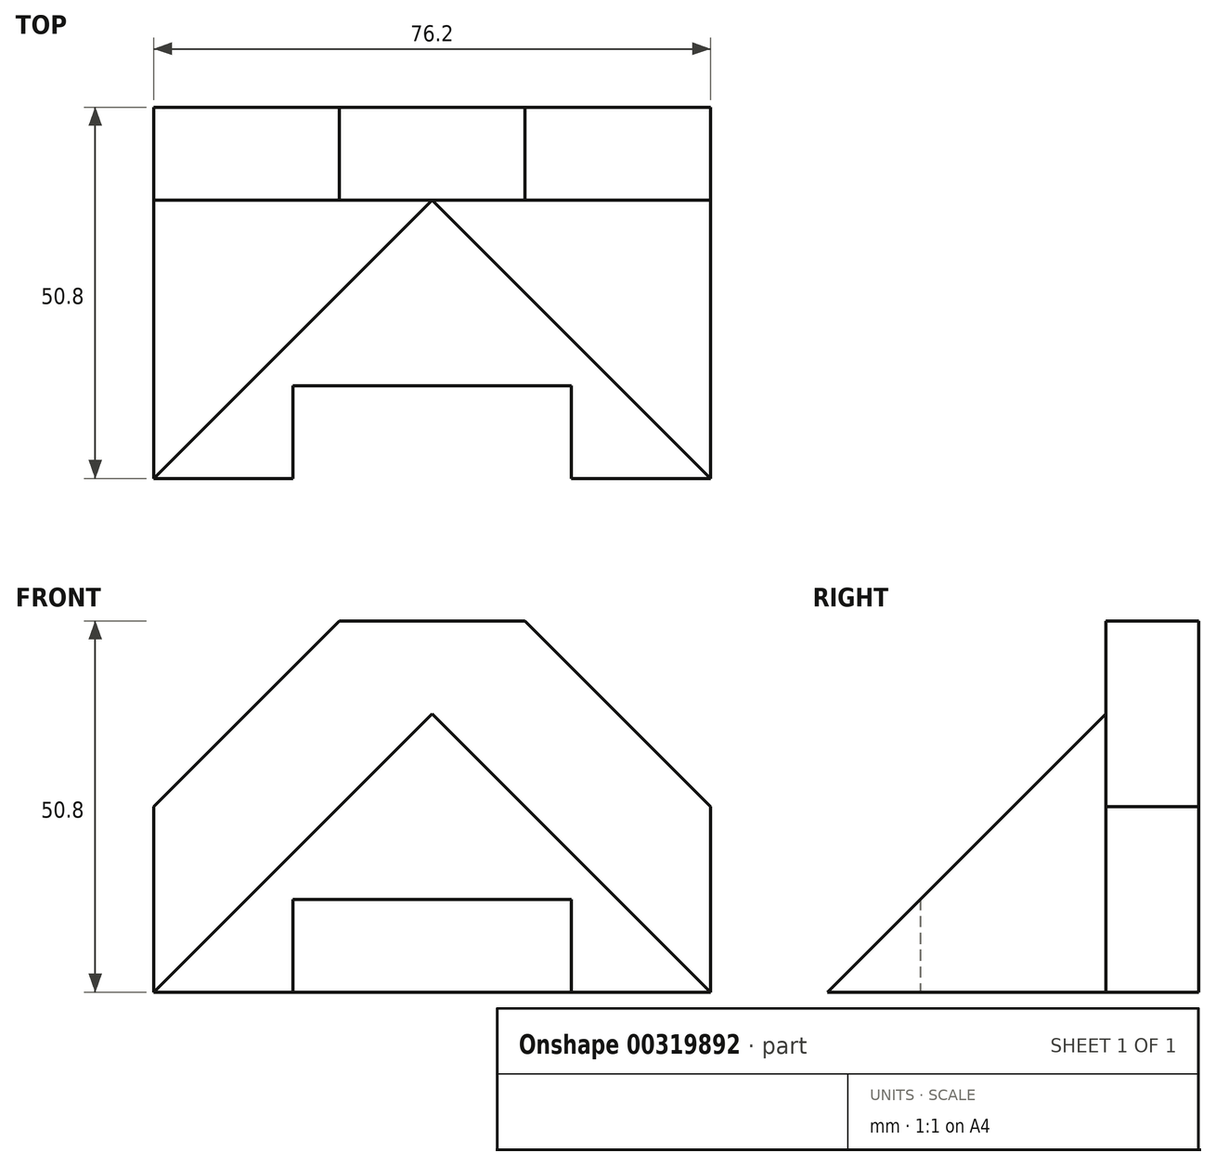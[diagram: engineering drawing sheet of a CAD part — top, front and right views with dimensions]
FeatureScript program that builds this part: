
annotation { "Feature Type Name" : "Feature", "Feature Type Description" : "" }
export const myFeature = defineFeature(function(context is Context, id is Id, definition is map)
    precondition{}
    {
        {
            var Q0;
            Q0=qCreatedBy(makeId("Front.planeOp"),FACE);
            var sketch = newSketch(context, id + "F0", { "sketchPlane" : qUnion([Q0])});
            skLineSegment(sketch, "E0", {"start": v(0, 0) * mm, "end": v(0, 50.8) * mm});
            skLineSegment(sketch, "E1", {"start": v(0, 50.8) * mm, "end": v(76.2, 50.8) * mm});
            skLineSegment(sketch, "E2", {"start": v(76.2, 50.8) * mm, "end": v(76.2, 0) * mm});
            skLineSegment(sketch, "E3", {"start": v(76.2, 0) * mm, "end": v(0, 0) * mm});
            skSolve(sketch);
        }
        {
            var Q0;
            Q0 = qSketchRegion(id + "F0", true);
            extrude(context, id + "F1", {"entities" : qUnion([Q0]), "depth" : 50.8 * mm});
        }
        {
            var Q0;
            Q0=makeQuery(id+"F1.opExtrude","SWEPT_FACE",FACE,{"disambiguationData":[OSD([sQuery(id+"F0.wireOp",EDGE,"E2")])]});
            var sketch = newSketch(context, id + "F2", { "sketchPlane" : qUnion([Q0])});
            skLineSegment(sketch, "E4", {"start": v(-50.8, 0) * mm, "end": v(-12.7, 38.1) * mm});
            skLineSegment(sketch, "E5", {"start": v(-12.7, 38.1) * mm, "end": v(-12.7, 50.8) * mm});
            skLineSegment(sketch, "E6", {"start": v(-12.7, 50.8) * mm, "end": v(-50.8, 50.8) * mm});
            skLineSegment(sketch, "E7", {"start": v(-50.8, 50.8) * mm, "end": v(-50.8, 0) * mm});
            skPoint(sketch, "E8", {"position": v(-12.7, 0) * mm});
            skSolve(sketch);
        }
        {
            var Q0;
            Q0 = qSketchRegion(id + "F2", true);
            extrude(context, id + "F3", {"entities" : qUnion([Q0]), "operationType" : NewBodyOperationType.REMOVE, "endBound" : BoundingType.THROUGH_ALL, "oppositeDirection" : true, "depth" : 25.4 * mm});
        }
        {
            var Q0;
            Q0=makeQuery(id+"F1.opExtrude","SWEPT_FACE",FACE,{"disambiguationData":[OSD([sQuery(id+"F0.wireOp",EDGE,"E3")])]});
            var sketch = newSketch(context, id + "F4", { "sketchPlane" : qUnion([Q0])});
            skLineSegment(sketch, "E9", {"start": v(19.05, 50.8) * mm, "end": v(19.05, 38.1) * mm});
            skLineSegment(sketch, "E10", {"start": v(19.05, 38.1) * mm, "end": v(57.15, 38.1) * mm});
            skLineSegment(sketch, "E11", {"start": v(57.15, 38.1) * mm, "end": v(57.15, 50.8) * mm});
            skLineSegment(sketch, "E12", {"start": v(57.15, 50.8) * mm, "end": v(19.05, 50.8) * mm});
            skLineSegment(sketch, "E13", {"start": v(0, 50.8) * mm, "end": v(19.05, 38.1) * mm, "construction": true});
            skLineSegment(sketch, "E14", {"start": v(57.15, 38.1) * mm, "end": v(76.2, 50.8) * mm, "construction": true});
            skSolve(sketch);
        }
        {
            var Q0;
            Q0 = qSketchRegion(id + "F4", true);
            extrude(context, id + "F5", {"entities" : qUnion([Q0]), "operationType" : NewBodyOperationType.REMOVE, "endBound" : BoundingType.THROUGH_ALL, "oppositeDirection" : true, "depth" : 25.4 * mm});
        }
        {
            var Q0;
            Q0=qCreatedBy(makeId("Front.planeOp"),FACE);
            cPlane(context, id + "F6", {"entities" : qUnion([Q0]), "cplaneType" : CPlaneType.OFFSET, "offset" : 50.8 * mm, "width" : 152.4 * mm, "height" : 152.4 * mm});
        }
        {
            var Q0;
            Q0=qCreatedBy(id+"F6.planeOp",FACE);
            var sketch = newSketch(context, id + "F7", { "sketchPlane" : qUnion([Q0])});
            skLineSegment(sketch, "E15", {"start": v(0, 0) * mm, "end": v(38.1, 38.1) * mm});
            skLineSegment(sketch, "E16", {"start": v(38.1, 38.1) * mm, "end": v(76.2, 0) * mm});
            skLineSegment(sketch, "E17", {"start": v(76.2, 0) * mm, "end": v(76.2, 38.1) * mm});
            skLineSegment(sketch, "E18", {"start": v(76.2, 38.1) * mm, "end": v(0, 38.1) * mm});
            skLineSegment(sketch, "E19", {"start": v(0, 38.1) * mm, "end": v(0, 0) * mm});
            skSolve(sketch);
        }
        {
            var Q0;
            Q0 = qSketchRegion(id + "F7", true);
            extrude(context, id + "F8", {"entities" : qUnion([Q0]), "operationType" : NewBodyOperationType.REMOVE, "oppositeDirection" : true, "depth" : 38.1 * mm});
        }
        {
            var Q0;
            Q0=makeQuery(id+"F1.opExtrude","CAP_FACE",FACE,{"disambiguationData":[OSD([sQuery(id+"F0.wireOp",EDGE,"E0"),sQuery(id+"F0.wireOp",EDGE,"E1"),sQuery(id+"F0.wireOp",EDGE,"E2"),sQuery(id+"F0.wireOp",EDGE,"E3")])],"isStart":true});
            var sketch = newSketch(context, id + "F9", { "sketchPlane" : qUnion([Q0])});
            skLineSegment(sketch, "E20", {"start": v(-50.8, 50.8) * mm, "end": v(-25.4, 50.8) * mm});
            skLineSegment(sketch, "E21", {"start": v(-25.4, 50.8) * mm, "end": v(0, 25.4) * mm});
            skLineSegment(sketch, "E22", {"start": v(-50.8, 50.8) * mm, "end": v(-76.2, 25.4) * mm});
            skLineSegment(sketch, "E23", {"start": v(-76.2, 25.4) * mm, "end": v(-76.2, 50.8) * mm});
            skLineSegment(sketch, "E24", {"start": v(-76.2, 50.8) * mm, "end": v(-50.8, 50.8) * mm});
            skLineSegment(sketch, "E25", {"start": v(-25.4, 50.8) * mm, "end": v(0, 50.8) * mm});
            skLineSegment(sketch, "E26", {"start": v(0, 25.4) * mm, "end": v(0, 50.8) * mm});
            skSolve(sketch);
        }
        {
            var Q0;
            Q0 = qSketchRegion(id + "F9", true);
            extrude(context, id + "F10", {"entities" : qUnion([Q0]), "operationType" : NewBodyOperationType.REMOVE, "oppositeDirection" : true, "depth" : 25.4 * mm});
        }
    });
